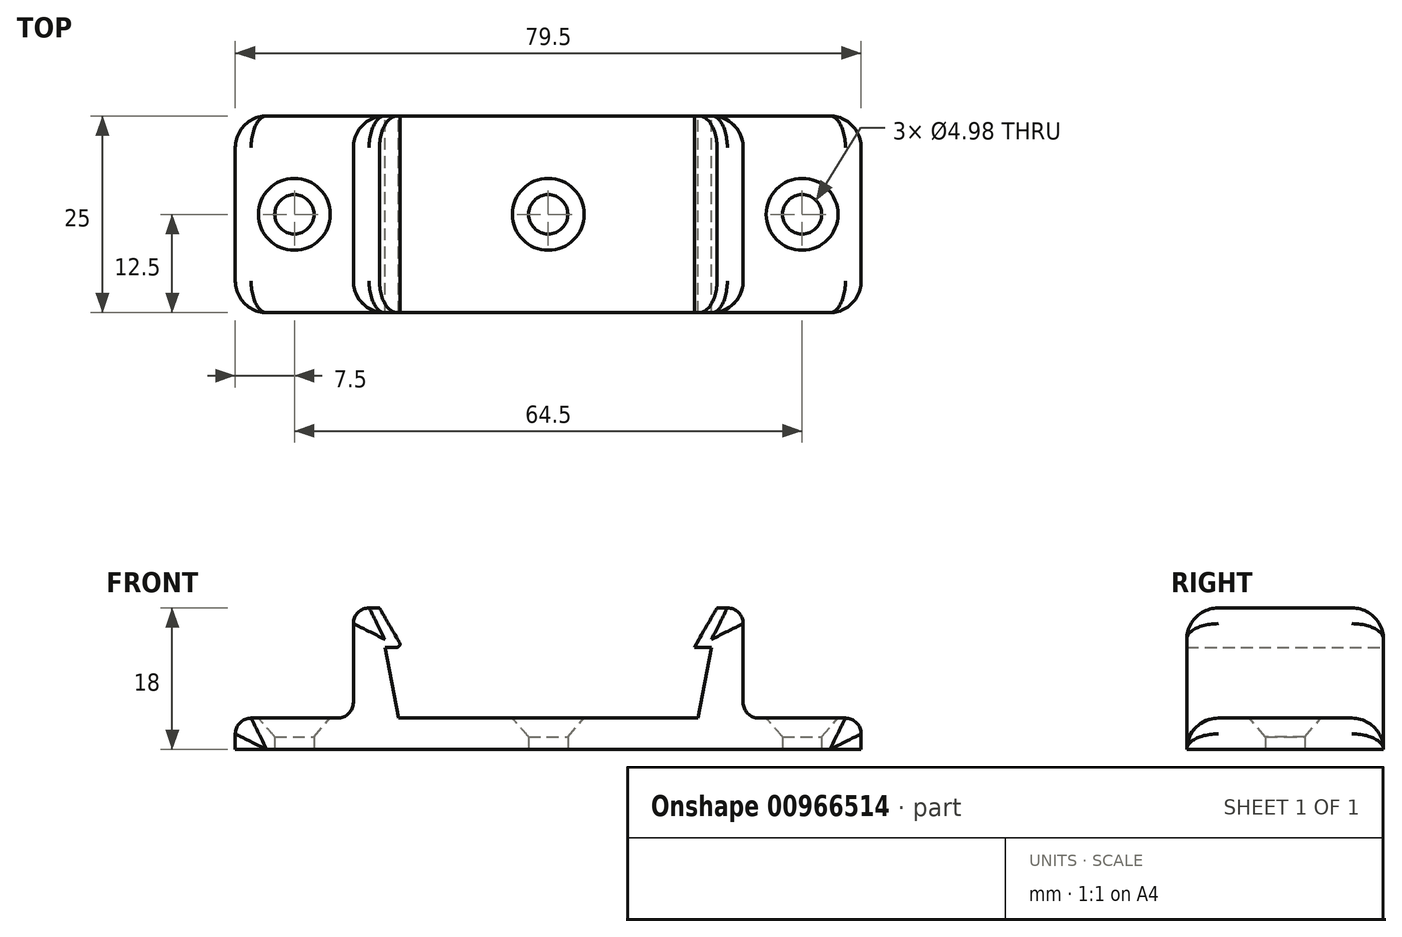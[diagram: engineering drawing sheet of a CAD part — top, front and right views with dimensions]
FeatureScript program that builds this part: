
annotation { "Feature Type Name" : "Feature", "Feature Type Description" : "" }
export const myFeature = defineFeature(function(context is Context, id is Id, definition is map)
    precondition{}
    {
        {
            var Q0;
            Q0=qCreatedBy(makeId("Front.planeOp"),FACE);
            var sketch = newSketch(context, id + "F0", { "sketchPlane" : qUnion([Q0])});
            skLineSegment(sketch, "E0", {"start": v(0, 35.15) * mm, "end": v(0, 0) * mm, "construction": true});
            skLineSegment(sketch, "E1", {"start": v(0, 0) * mm, "end": v(24.75, 0) * mm});
            skLineSegment(sketch, "E2", {"start": v(24.75, 6) * mm, "end": v(24.75, 16) * mm});
            skLineSegment(sketch, "E3", {"start": v(22.75, 18) * mm, "end": v(21.44, 18) * mm});
            skLineSegment(sketch, "E4", {"start": v(21.44, 18) * mm, "end": v(18.55, 13) * mm});
            skLineSegment(sketch, "E5", {"start": v(18.55, 13) * mm, "end": v(20.75, 13) * mm});
            skLineSegment(sketch, "E6", {"start": v(20.75, 13) * mm, "end": v(19, 4) * mm});
            skLineSegment(sketch, "E7", {"start": v(19, 4) * mm, "end": v(0, 4) * mm});
            skLineSegment(sketch, "E8.bottom", {"start": v(24.75, 0) * mm, "end": v(39.75, 0) * mm});
            skLineSegment(sketch, "E8.top", {"start": v(26.75, 4) * mm, "end": v(37.75, 4) * mm});
            skLineSegment(sketch, "E8.right", {"start": v(39.75, 0) * mm, "end": v(39.75, 2) * mm});
            skPoint(sketch, "E9.visualSharp", {"position": v(39.75, 4) * mm});
            skArc(sketch, "E9.filletArc", {"start": v(39.75, 2) * mm, "mid": v(39.16, 3.41) * mm, "end": v(37.75, 4) * mm});
            skPoint(sketch, "E10.visualSharp", {"position": v(24.75, 4) * mm});
            skArc(sketch, "E10.filletArc", {"start": v(24.75, 6) * mm, "mid": v(25.34, 4.59) * mm, "end": v(26.75, 4) * mm});
            skPoint(sketch, "E11.visualSharp", {"position": v(24.75, 18) * mm});
            skArc(sketch, "E11.filletArc", {"start": v(24.75, 16) * mm, "mid": v(24.16, 17.41) * mm, "end": v(22.75, 18) * mm});
            skLineSegment(sketch, "E12.MirrorCS", {"start": v(-22.75, 18) * mm, "end": v(-21.44, 18) * mm});
            skLineSegment(sketch, "E13.MirrorCS", {"start": v(-18.55, 13) * mm, "end": v(-20.75, 13) * mm});
            skPoint(sketch, "E14.MirrorP", {"position": v(-24.75, 18) * mm});
            skLineSegment(sketch, "E15.MirrorCS", {"start": v(-24.75, 6) * mm, "end": v(-24.75, 16) * mm});
            skLineSegment(sketch, "E16.MirrorCS", {"start": v(-20.75, 13) * mm, "end": v(-19, 4) * mm});
            skLineSegment(sketch, "E17.MirrorCS", {"start": v(-39.75, 0) * mm, "end": v(-39.75, 2) * mm});
            skLineSegment(sketch, "E18.MirrorCS", {"start": v(-26.75, 4) * mm, "end": v(-37.75, 4) * mm});
            skLineSegment(sketch, "E19.MirrorCS", {"start": v(0, 0) * mm, "end": v(-24.75, 0) * mm});
            skArc(sketch, "E20.MirrorCS", {"start": v(-39.75, 2) * mm, "mid": v(-39.16, 3.41) * mm, "end": v(-37.75, 4) * mm});
            skArc(sketch, "E21.MirrorCS", {"start": v(-24.75, 6) * mm, "mid": v(-25.34, 4.59) * mm, "end": v(-26.75, 4) * mm});
            skArc(sketch, "E22.MirrorCS", {"start": v(-24.75, 16) * mm, "mid": v(-24.16, 17.41) * mm, "end": v(-22.75, 18) * mm});
            skPoint(sketch, "E23.MirrorP", {"position": v(-39.75, 4) * mm});
            skPoint(sketch, "E24.MirrorP", {"position": v(-24.75, 4) * mm});
            skLineSegment(sketch, "E25.MirrorCS", {"start": v(-24.75, 0) * mm, "end": v(-39.75, 0) * mm});
            skLineSegment(sketch, "E26.MirrorCS", {"start": v(-19, 4) * mm, "end": v(0, 4) * mm});
            skLineSegment(sketch, "E27.MirrorCS", {"start": v(-21.44, 18) * mm, "end": v(-18.55, 13) * mm});
            skSolve(sketch);
        }
        {
            var Q0;
            Q0=qSketchRegion(id+"F0",true);
            extrude(context, id + "F1", {"entities" : qUnion([Q0]), "depth" : 25 * mm, "offsetDistance" : 25 * mm});
        }
        {
            var Q0;
            Q0=makeQuery(id+"F1.opExtrude","SWEPT_FACE",FACE,{"disambiguationData":[OSD([sQuery(id+"F0.wireOp",EDGE,"E7"),sQuery(id+"F0.wireOp",EDGE,"E26.MirrorCS")])]});
            var sketch = newSketch(context, id + "F2", { "sketchPlane" : qUnion([Q0])});
            skLineSegment(sketch, "E28", {"start": v(0, -25) * mm, "end": v(0, 0) * mm, "construction": true});
            skPoint(sketch, "E29", {"position": v(0, -12.5) * mm});
            skLineSegment(sketch, "E30.0", {"start": v(-26.75, -25) * mm, "end": v(-26.75, 0) * mm, "construction": true});
            skLineSegment(sketch, "E30.1", {"start": v(-37.75, -25) * mm, "end": v(-37.75, 0) * mm, "construction": true});
            skLineSegment(sketch, "E30.2", {"start": v(26.75, -25) * mm, "end": v(26.75, 0) * mm, "construction": true});
            skLineSegment(sketch, "E30.3", {"start": v(37.75, -25) * mm, "end": v(37.75, 0) * mm, "construction": true});
            skLineSegment(sketch, "E31", {"start": v(-37.75, -12.5) * mm, "end": v(-26.75, -12.5) * mm, "construction": true});
            skLineSegment(sketch, "E32", {"start": v(26.75, -12.5) * mm, "end": v(37.75, -12.5) * mm, "construction": true});
            skPoint(sketch, "E33", {"position": v(-32.25, -12.5) * mm});
            skPoint(sketch, "E34", {"position": v(32.25, -12.5) * mm});
            skSolve(sketch);
        }
        {
            var Q0;
            Q0=sQuery(id+"F2.wireOp",VERTEX,"E33");
            var Q1;
            Q1=sQuery(id+"F2.wireOp",VERTEX,"E29");
            var Q2;
            Q2=sQuery(id+"F2.wireOp",VERTEX,"E34");
            var Q3;
            Q3=makeQuery(id+"F1.opExtrude","SWEPT_BODY",BODY,{"disambiguationData":[OSD([sQuery(id+"F0.wireOp",EDGE,"E1"),sQuery(id+"F0.wireOp",EDGE,"E2"),sQuery(id+"F0.wireOp",EDGE,"E3"),sQuery(id+"F0.wireOp",EDGE,"E4"),sQuery(id+"F0.wireOp",EDGE,"E5"),sQuery(id+"F0.wireOp",EDGE,"E6"),sQuery(id+"F0.wireOp",EDGE,"E7"),sQuery(id+"F0.wireOp",EDGE,"E8.bottom"),sQuery(id+"F0.wireOp",EDGE,"E8.top"),sQuery(id+"F0.wireOp",EDGE,"E8.right"),sQuery(id+"F0.wireOp",EDGE,"E9.filletArc"),sQuery(id+"F0.wireOp",EDGE,"E10.filletArc"),sQuery(id+"F0.wireOp",EDGE,"E11.filletArc"),sQuery(id+"F0.wireOp",EDGE,"E12.MirrorCS"),sQuery(id+"F0.wireOp",EDGE,"E13.MirrorCS"),sQuery(id+"F0.wireOp",EDGE,"E15.MirrorCS"),sQuery(id+"F0.wireOp",EDGE,"E16.MirrorCS"),sQuery(id+"F0.wireOp",EDGE,"E17.MirrorCS"),sQuery(id+"F0.wireOp",EDGE,"E18.MirrorCS"),sQuery(id+"F0.wireOp",EDGE,"E19.MirrorCS"),sQuery(id+"F0.wireOp",EDGE,"E20.MirrorCS"),sQuery(id+"F0.wireOp",EDGE,"E21.MirrorCS"),sQuery(id+"F0.wireOp",EDGE,"E22.MirrorCS"),sQuery(id+"F0.wireOp",EDGE,"E25.MirrorCS"),sQuery(id+"F0.wireOp",EDGE,"E26.MirrorCS"),sQuery(id+"F0.wireOp",EDGE,"E27.MirrorCS")])]});
            hole(context, id + "F3", {"style" : HoleStyle.C_SINK, "endStyle" : HoleEndStyle.THROUGH, "standardTappedOrClearance" : lookupTablePath({ "fit" : "Normal (ASME)", "standard" : "ANSI", "size" : "#8", "type" : "Clearance" }), "standardBlindInLast" : lookupTablePath({ "fit" : "Normal", "standard" : "ANSI", "size" : "#8", "type" : "Clearance" }), "holeDiameter" : 4.98 * mm, "cSinkDiameter" : 9.12 * mm, "cSinkAngle" : 82 * degree, "majorDiameter" : 5 * mm, "isTappedThrough" : true, "tappedDepth" : 12 * mm, "tapClearance" : 3, "locations" : qUnion([Q0, Q1, Q2]), "scope" : qUnion([Q3]), "startStyle" : HoleStartStyle.PART});
        }
        {
            var Q0;
            Q0=makeQuery(id+"F1.opExtrude","CAP_EDGE",EDGE,{"disambiguationData":[OSD([sQuery(id+"F0.wireOp",EDGE,"E8.right")])],"isStart":true});
            var Q1;
            Q1=makeQuery(id+"F1.opExtrude","CAP_EDGE",EDGE,{"disambiguationData":[OSD([sQuery(id+"F0.wireOp",EDGE,"E18.MirrorCS")])],"isStart":true});
            var Q2;
            Q2=makeQuery(id+"F1.opExtrude","CAP_EDGE",EDGE,{"disambiguationData":[OSD([sQuery(id+"F0.wireOp",EDGE,"E18.MirrorCS")])],"isStart":false});
            var Q3;
            Q3=makeQuery(id+"F1.opExtrude","CAP_EDGE",EDGE,{"disambiguationData":[OSD([sQuery(id+"F0.wireOp",EDGE,"E8.top")])],"isStart":false});
            fillet(context, id + "F4", {"entities" : qUnion([Q0, Q1, Q2, Q3]), "radius" : 4 * mm, "tangentPropagation" : true, "allowEdgeOverflow" : false});
        }
        {
            var Q0;
            Q0=makeQuery(id+"F1.opExtrude","SWEPT_EDGE",EDGE,{"disambiguationData":[OSD([sQuery(id+"F0.wireOp",EDGE,"E13.MirrorCS"),sQuery(id+"F0.wireOp",EDGE,"E27.MirrorCS")])]});
            fillet(context, id + "F5", {"entities" : qUnion([Q0]), "radius" : 0.4 * mm, "tangentPropagation" : true, "allowEdgeOverflow" : false});
        }
    });
